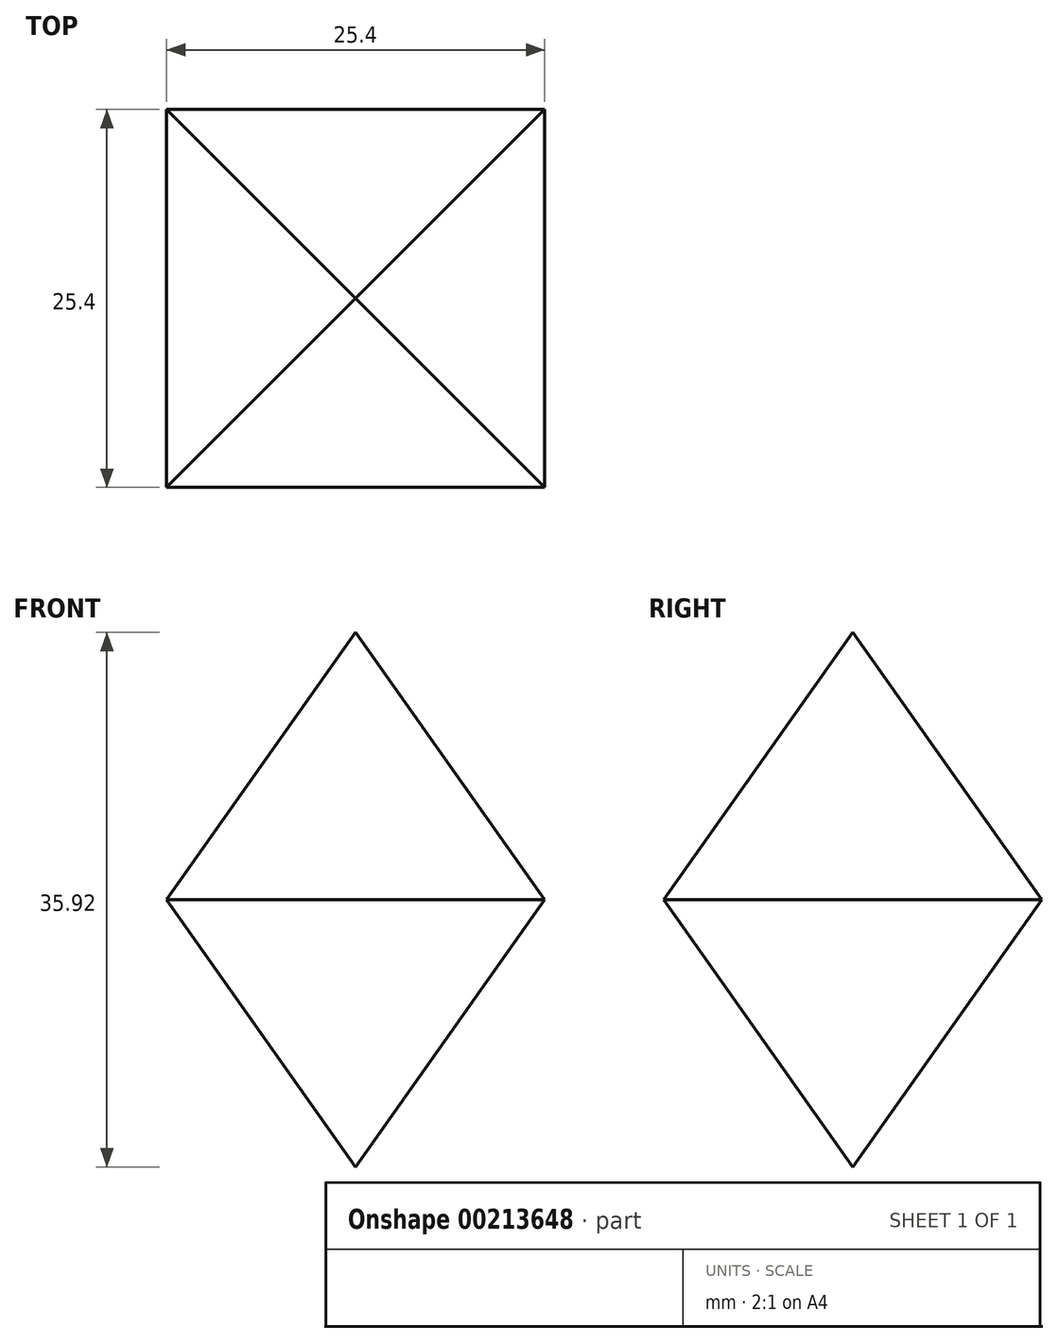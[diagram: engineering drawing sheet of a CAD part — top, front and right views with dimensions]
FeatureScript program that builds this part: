
annotation { "Feature Type Name" : "Feature", "Feature Type Description" : "" }
export const myFeature = defineFeature(function(context is Context, id is Id, definition is map)
    precondition{}
    {
        {
            var Q0;
            Q0=qCreatedBy(makeId("Top.planeOp"),FACE);
            var sketch = newSketch(context, id + "F0", { "sketchPlane" : qUnion([Q0])});
            skCircle(sketch, "E0.cCircle", {"center": v(0, 0) * mm, "radius": 12.7 * mm, "construction": true});
            skLineSegment(sketch, "E0.0", {"start": v(12.7, 12.7) * mm, "end": v(12.7, -12.7) * mm});
            skLineSegment(sketch, "E0.1", {"start": v(12.7, -12.7) * mm, "end": v(-12.7, -12.7) * mm});
            skLineSegment(sketch, "E0.2", {"start": v(-12.7, -12.7) * mm, "end": v(-12.7, 12.7) * mm});
            skLineSegment(sketch, "E0.3", {"start": v(-12.7, 12.7) * mm, "end": v(12.7, 12.7) * mm});
            skPoint(sketch, "E0.0.midPoint", {"position": v(12.7, 0) * mm});
            skSolve(sketch);
        }
        {
            var Q0;
            Q0=qCreatedBy(makeId("Front.planeOp"),FACE);
            var sketch = newSketch(context, id + "F1", { "sketchPlane" : qUnion([Q0])});
            skPoint(sketch, "E1", {"position": v(0, 17.96) * mm});
            skPoint(sketch, "E2", {"position": v(0, -17.96) * mm});
            skSolve(sketch);
        }
        {
            var Q0;
            Q0=makeQuery(id+"F0.imprint","IMPRINT",FACE,{"disambiguationData":[TD([[makeQuery(id+"F0.imprint","IMPRINT",EDGE,{"derivedFrom":sQuery(id+"F0.wireOp",EDGE,"E0.0")}),-1.0]])]});
            var Q1;
            Q1=sQuery(id+"F1.wireOp",VERTEX,"E1");
            loft(context, id + "F2", {"sheetProfilesArray" : [{ "sheetProfileEntities" : qUnion([Q0]) }, { "sheetProfileEntities" : qUnion([Q1]) }]});
        }
        {
            var Q1;
            Q1 = qSketchRegion(id + "F0", true);
            var Q2;
            Q2=sQuery(id+"F1.wireOp",VERTEX,"E2");
            loft(context, id + "F3", {"operationType" : NewBodyOperationType.ADD, "sheetProfilesArray" : [{ "sheetProfileEntities" : qUnion([Q1]) }, { "sheetProfileEntities" : qUnion([Q2]) }]});
        }
    });
